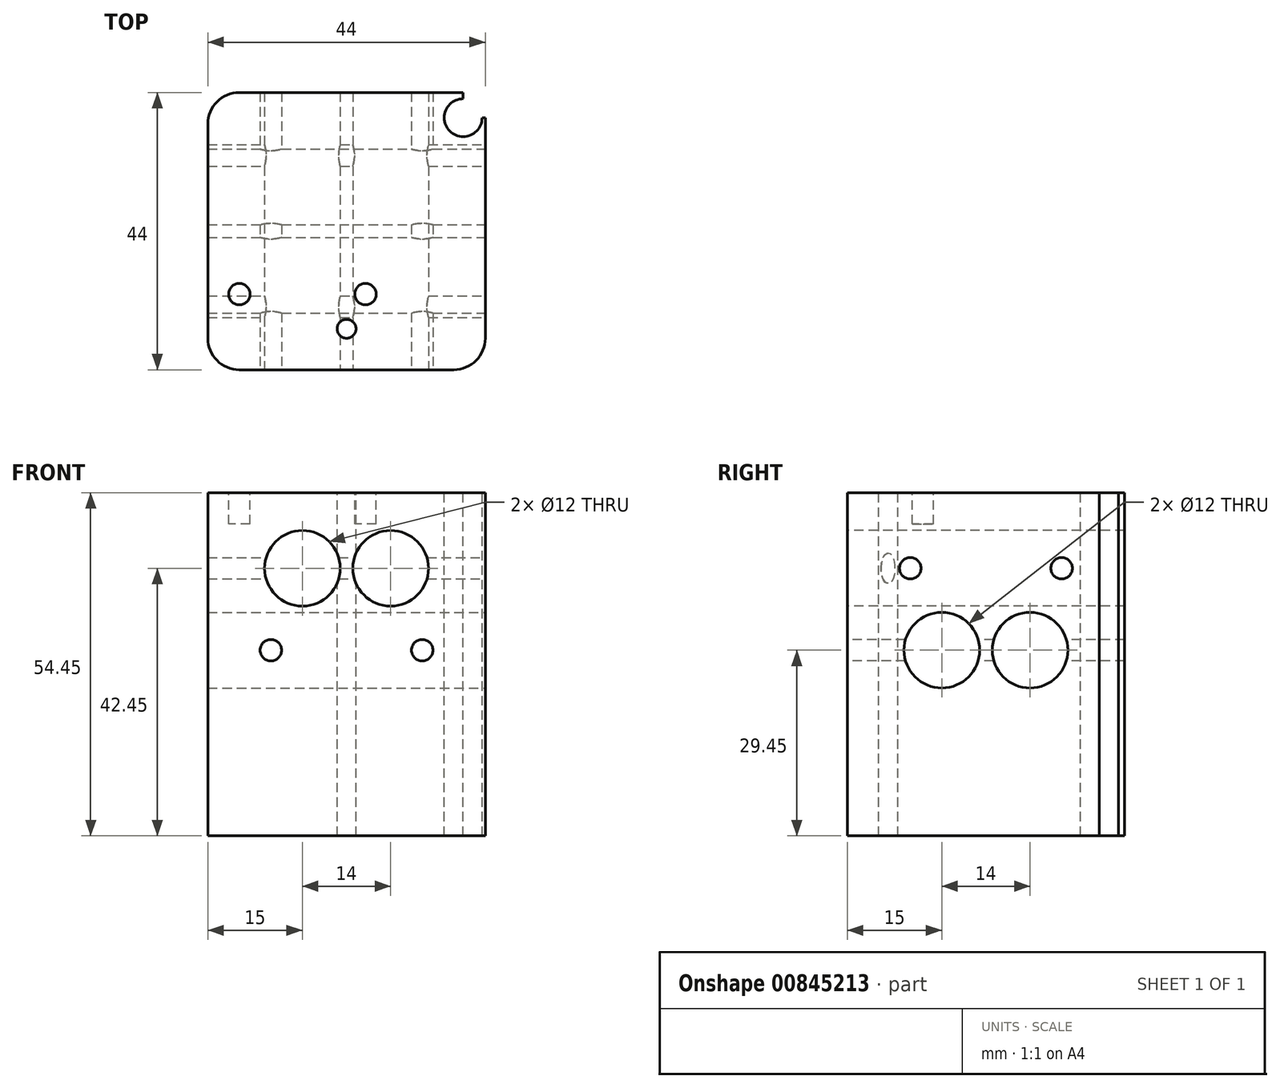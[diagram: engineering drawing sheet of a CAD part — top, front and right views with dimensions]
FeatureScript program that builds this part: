
annotation { "Feature Type Name" : "Feature", "Feature Type Description" : "" }
export const myFeature = defineFeature(function(context is Context, id is Id, definition is map)
    precondition{}
    {
        {
            var Q0;
            Q0=qCreatedBy(makeId("Top.planeOp"),FACE);
            var sketch = newSketch(context, id + "F0", { "sketchPlane" : qUnion([Q0])});
            skLineSegment(sketch, "E0.bottom", {"start": v(-22, 22) * mm, "end": v(22, 22) * mm});
            skLineSegment(sketch, "E0.top", {"start": v(-22, -22) * mm, "end": v(22, -22) * mm});
            skLineSegment(sketch, "E0.left", {"start": v(-22, 22) * mm, "end": v(-22, -22) * mm});
            skLineSegment(sketch, "E0.right", {"start": v(22, 22) * mm, "end": v(22, -22) * mm});
            skPoint(sketch, "E0.middle", {"position": v(0, 0) * mm});
            skCircle(sketch, "E1", {"center": v(18.5, 18) * mm, "radius": 3 * mm});
            skLineSegment(sketch, "E2", {"start": v(18.5, 18) * mm, "end": v(18.5, 22) * mm});
            skLineSegment(sketch, "E3", {"start": v(18.5, 18) * mm, "end": v(22, 18) * mm});
            skCircle(sketch, "E4", {"center": v(-17, -10) * mm, "radius": 1.7 * mm});
            skCircle(sketch, "E5", {"center": v(0, -15.5) * mm, "radius": 1.5 * mm});
            skCircle(sketch, "E6", {"center": v(3, -10) * mm, "radius": 1.7 * mm});
            skLineSegment(sketch, "E7", {"start": v(-22, -10) * mm, "end": v(22, -10) * mm, "construction": true});
            skSolve(sketch);
        }
        {
            var Q0;
            {var subQ1=sQuery(id+"F0.wireOp",EDGE,"E0.top");Q0=makeQuery(id+"F0.imprint","IMPRINT",FACE,{"disambiguationData":[TD([[makeQuery(id+"F0.imprint","IMPRINT",EDGE,{"derivedFrom":subQ1}),1.0]])]});}
            var Q1;
            Q1=makeQuery(id+"F0.imprint","IMPRINT",FACE,{"disambiguationData":[TD([[makeQuery(id+"F0.imprint","IMPRINT",EDGE,{"derivedFrom":sQuery(id+"F0.wireOp",EDGE,"E4")}),1.0]])]});
            var Q2;
            Q2=makeQuery(id+"F0.imprint","IMPRINT",FACE,{"disambiguationData":[TD([[makeQuery(id+"F0.imprint","IMPRINT",EDGE,{"derivedFrom":sQuery(id+"F0.wireOp",EDGE,"E5")}),1.0]])]});
            var Q3;
            Q3=makeQuery(id+"F0.imprint","IMPRINT",FACE,{"disambiguationData":[TD([[makeQuery(id+"F0.imprint","IMPRINT",EDGE,{"derivedFrom":sQuery(id+"F0.wireOp",EDGE,"E6")}),1.0]])]});
            extrude(context, id + "F1", {"entities" : qUnion([Q0, Q1, Q2, Q3]), "oppositeDirection" : true, "depth" : 54.45 * mm, "offsetDistance" : 25 * mm});
        }
        {
            var Q0;
            Q0=makeQuery(id+"F1.opExtrude","SWEPT_FACE",FACE,{"disambiguationData":[OSD([sQuery(id+"F0.wireOp",EDGE,"E0.top")])]});
            var sketch = newSketch(context, id + "F2", { "sketchPlane" : qUnion([Q0])});
            skCircle(sketch, "E8", {"center": v(-12, -25) * mm, "radius": 1.7 * mm});
            skCircle(sketch, "E9", {"center": v(12, -25) * mm, "radius": 1.7 * mm});
            skCircle(sketch, "E10", {"center": v(-7, -12) * mm, "radius": 6 * mm});
            skCircle(sketch, "E11", {"center": v(7, -12) * mm, "radius": 6 * mm});
            skSolve(sketch);
        }
        {
            var Q0;
            Q0=makeQuery(id+"F2.imprint","IMPRINT",FACE,{"disambiguationData":[TD([[makeQuery(id+"F2.imprint","IMPRINT",EDGE,{"derivedFrom":sQuery(id+"F2.wireOp",EDGE,"E8")}),1.0]])]});
            var Q1;
            Q1=makeQuery(id+"F2.imprint","IMPRINT",FACE,{"disambiguationData":[TD([[makeQuery(id+"F2.imprint","IMPRINT",EDGE,{"derivedFrom":sQuery(id+"F2.wireOp",EDGE,"E9")}),1.0]])]});
            var Q2;
            Q2=makeQuery(id+"F2.imprint","IMPRINT",FACE,{"disambiguationData":[TD([[makeQuery(id+"F2.imprint","IMPRINT",EDGE,{"derivedFrom":sQuery(id+"F2.wireOp",EDGE,"E10")}),1.0]])]});
            var Q3;
            Q3=makeQuery(id+"F2.imprint","IMPRINT",FACE,{"disambiguationData":[TD([[makeQuery(id+"F2.imprint","IMPRINT",EDGE,{"derivedFrom":sQuery(id+"F2.wireOp",EDGE,"E11")}),1.0]])]});
            extrude(context, id + "F3", {"entities" : qUnion([Q0, Q1, Q2, Q3]), "operationType" : NewBodyOperationType.REMOVE, "oppositeDirection" : true, "depth" : 44 * mm, "offsetDistance" : 25 * mm});
        }
        {
            var Q0;
            Q0=makeQuery(id+"F1.opExtrude","SWEPT_FACE",FACE,{"disambiguationData":[OSD([sQuery(id+"F0.wireOp",EDGE,"E0.right")])]});
            var sketch = newSketch(context, id + "F4", { "sketchPlane" : qUnion([Q0])});
            skCircle(sketch, "E12", {"center": v(-12, -12) * mm, "radius": 1.7 * mm});
            skCircle(sketch, "E13", {"center": v(12, -12) * mm, "radius": 1.7 * mm});
            skCircle(sketch, "E14", {"center": v(-7, -25) * mm, "radius": 6 * mm});
            skCircle(sketch, "E15", {"center": v(7, -25) * mm, "radius": 6 * mm});
            skSolve(sketch);
        }
        {
            var Q0;
            Q0=makeQuery(id+"F4.imprint","IMPRINT",FACE,{"disambiguationData":[TD([[makeQuery(id+"F4.imprint","IMPRINT",EDGE,{"derivedFrom":sQuery(id+"F4.wireOp",EDGE,"E12")}),1.0]])]});
            var Q1;
            Q1=makeQuery(id+"F4.imprint","IMPRINT",FACE,{"disambiguationData":[TD([[makeQuery(id+"F4.imprint","IMPRINT",EDGE,{"derivedFrom":sQuery(id+"F4.wireOp",EDGE,"E13")}),1.0]])]});
            var Q2;
            Q2=makeQuery(id+"F4.imprint","IMPRINT",FACE,{"disambiguationData":[TD([[makeQuery(id+"F4.imprint","IMPRINT",EDGE,{"derivedFrom":sQuery(id+"F4.wireOp",EDGE,"E14")}),1.0]])]});
            var Q3;
            Q3=makeQuery(id+"F4.imprint","IMPRINT",FACE,{"disambiguationData":[TD([[makeQuery(id+"F4.imprint","IMPRINT",EDGE,{"derivedFrom":sQuery(id+"F4.wireOp",EDGE,"E15")}),1.0]])]});
            extrude(context, id + "F5", {"entities" : qUnion([Q0, Q1, Q2, Q3]), "operationType" : NewBodyOperationType.REMOVE, "oppositeDirection" : true, "depth" : 44 * mm, "offsetDistance" : 25 * mm});
        }
        {
            var Q0;
            Q0=makeQuery(id+"F1.opExtrude","SWEPT_EDGE",EDGE,{"disambiguationData":[OSD([sQuery(id+"F0.wireOp",EDGE,"E0.top"),sQuery(id+"F0.wireOp",EDGE,"E0.right")])]});
            var Q1;
            Q1=makeQuery(id+"F1.opExtrude","SWEPT_EDGE",EDGE,{"disambiguationData":[OSD([sQuery(id+"F0.wireOp",EDGE,"E0.top"),sQuery(id+"F0.wireOp",EDGE,"E0.left")])]});
            var Q2;
            Q2=makeQuery(id+"F1.opExtrude","SWEPT_EDGE",EDGE,{"disambiguationData":[OSD([sQuery(id+"F0.wireOp",EDGE,"E0.bottom"),sQuery(id+"F0.wireOp",EDGE,"E0.left")])]});
            fillet(context, id + "F6", {"entities" : qUnion([Q0, Q1, Q2]), "radius" : 5 * mm, "tangentPropagation" : true, "allowEdgeOverflow" : false});
        }
        {
            var Q0;
            Q0=makeQuery(id+"F0.imprint","IMPRINT",FACE,{"disambiguationData":[TD([[makeQuery(id+"F0.imprint","IMPRINT",EDGE,{"derivedFrom":sQuery(id+"F0.wireOp",EDGE,"E5")}),1.0]])]});
            extrude(context, id + "F7", {"entities" : qUnion([Q0]), "operationType" : NewBodyOperationType.REMOVE, "oppositeDirection" : true, "depth" : 55 * mm, "offsetDistance" : 25 * mm});
        }
        {
            var Q0;
            Q0=makeQuery(id+"F0.imprint","IMPRINT",FACE,{"disambiguationData":[TD([[makeQuery(id+"F0.imprint","IMPRINT",EDGE,{"derivedFrom":sQuery(id+"F0.wireOp",EDGE,"E4")}),1.0]])]});
            var Q1;
            Q1=makeQuery(id+"F0.imprint","IMPRINT",FACE,{"disambiguationData":[TD([[makeQuery(id+"F0.imprint","IMPRINT",EDGE,{"derivedFrom":sQuery(id+"F0.wireOp",EDGE,"E6")}),1.0]])]});
            extrude(context, id + "F8", {"entities" : qUnion([Q0, Q1]), "operationType" : NewBodyOperationType.REMOVE, "oppositeDirection" : true, "depth" : 5 * mm, "offsetDistance" : 25 * mm});
        }
    });
